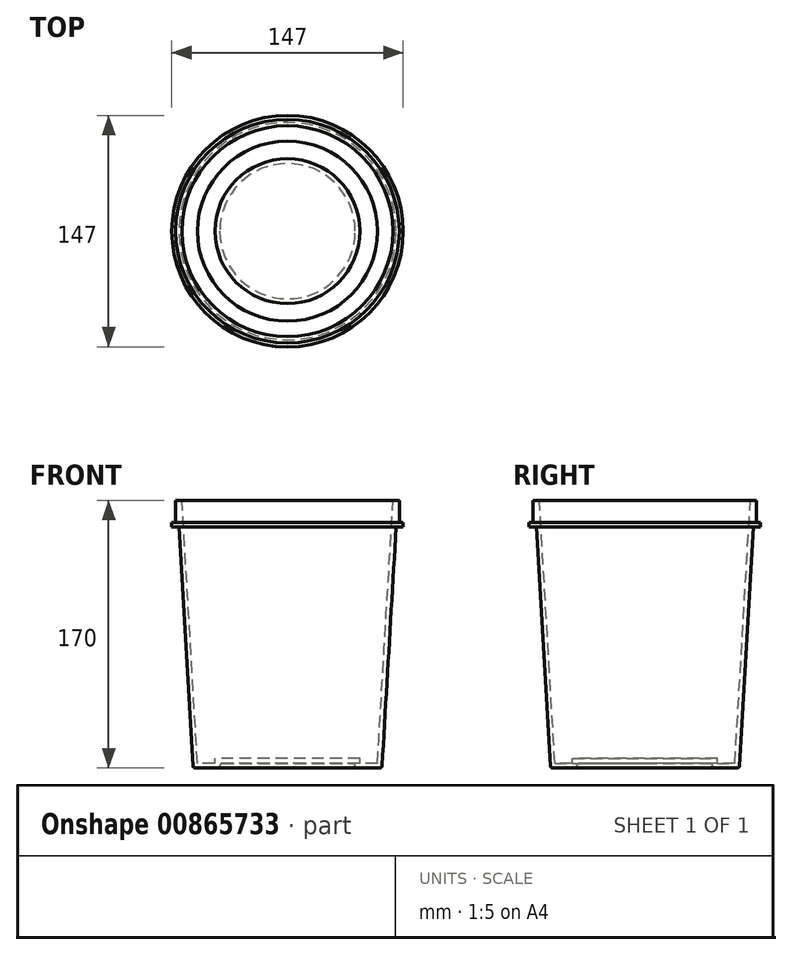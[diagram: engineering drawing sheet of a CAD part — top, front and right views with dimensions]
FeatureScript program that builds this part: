
annotation { "Feature Type Name" : "Feature", "Feature Type Description" : "" }
export const myFeature = defineFeature(function(context is Context, id is Id, definition is map)
    precondition{}
    {
        {
            var Q0;
            Q0=qCreatedBy(makeId("Right.planeOp"),FACE);
            var sketch = newSketch(context, id + "F0", { "sketchPlane" : qUnion([Q0])});
            skLineSegment(sketch, "E0", {"start": v(43, 0) * mm, "end": v(60, 0) * mm});
            skLineSegment(sketch, "E1", {"start": v(60, 0) * mm, "end": v(69, 153) * mm});
            skLineSegment(sketch, "E2", {"start": v(69, 153) * mm, "end": v(73.5, 153) * mm});
            skLineSegment(sketch, "E3", {"start": v(73.5, 153) * mm, "end": v(73.5, 156) * mm});
            skLineSegment(sketch, "E4", {"start": v(73.5, 156) * mm, "end": v(71, 156) * mm});
            skLineSegment(sketch, "E5", {"start": v(71, 156) * mm, "end": v(71, 170) * mm});
            skLineSegment(sketch, "E6", {"start": v(71, 170) * mm, "end": v(67, 170) * mm});
            skLineSegment(sketch, "E7", {"start": v(67, 170) * mm, "end": v(57.17, 3) * mm});
            skLineSegment(sketch, "E8", {"start": v(57.17, 3) * mm, "end": v(46, 3) * mm});
            skLineSegment(sketch, "E9", {"start": v(46, 3) * mm, "end": v(46, 6) * mm});
            skLineSegment(sketch, "E10", {"start": v(46, 6) * mm, "end": v(0, 6) * mm});
            skLineSegment(sketch, "E11", {"start": v(43, 0) * mm, "end": v(43, 3) * mm});
            skLineSegment(sketch, "E12.trimOffspring", {"start": v(43, 3) * mm, "end": v(0, 3) * mm});
            skLineSegment(sketch, "E13", {"start": v(0, 6) * mm, "end": v(0, 3) * mm});
            skSolve(sketch);
        }
        {
            var Q0;
            Q0=makeQuery(id+"F0.imprint","IMPRINT",FACE,{"disambiguationData":[TD([[makeQuery(id+"F0.imprint","IMPRINT",EDGE,{"derivedFrom":sQuery(id+"F0.wireOp",EDGE,"E0")}),1.0]])]});
            var Q1;
            Q1 = qConstructionFilter(qBodyType(qCreatedBy(id + "F0" ,EDGE), BodyType.WIRE), ConstructionObject.NO);
            var Q2;
            Q2=sQuery(id+"F0.wireOp",EDGE,"E13");
            revolve(context, id + "F1", {"surfaceOperationType" : NewSurfaceOperationType.NEW, "entities" : qUnion([Q0]), "surfaceEntities" : qUnion([Q1]), "axis" : qUnion([Q2]), "revolveType" : RevolveType.FULL});
        }
        {
            var Q0;
            Q0=makeQuery(id+"F1.opRevolve","SWEPT_FACE",FACE,{"disambiguationData":[OSD([sQuery(id+"F0.wireOp",EDGE,"E0")])]});
            var Q1;
            Q1=makeQuery(id+"F1.opRevolve","SWEPT_FACE",FACE,{"disambiguationData":[OSD([sQuery(id+"F0.wireOp",EDGE,"E12.trimOffspring")])]});
            fillet(context, id + "F2", {"entities" : qUnion([Q0, Q1]), "radius" : 1.5 * mm, "tangentPropagation" : true, "allowEdgeOverflow" : false});
        }
    });
